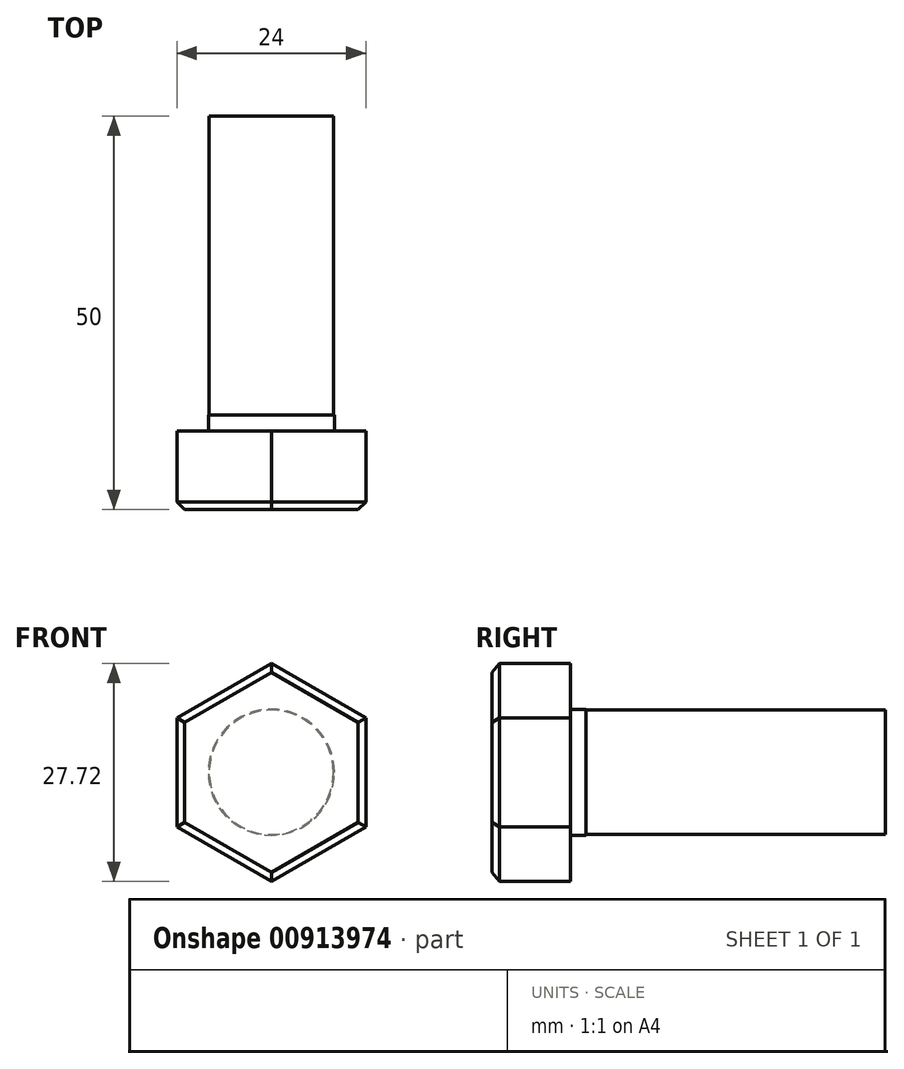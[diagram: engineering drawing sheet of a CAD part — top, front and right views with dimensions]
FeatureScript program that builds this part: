
annotation { "Feature Type Name" : "Feature", "Feature Type Description" : "" }
export const myFeature = defineFeature(function(context is Context, id is Id, definition is map)
    precondition{}
    {
        {
            var Q0;
            Q0=qCreatedBy(makeId("Front.planeOp"),FACE);
            var sketch = newSketch(context, id + "F0", { "sketchPlane" : qUnion([Q0])});
            skLineSegment(sketch, "E0", {"start": v(0, 45.9) * mm, "end": v(0, -43.11) * mm, "construction": true});
            skLineSegment(sketch, "E1", {"start": v(-56.15, 0) * mm, "end": v(55.88, 0) * mm, "construction": true});
            skCircle(sketch, "E2.cCircle", {"center": v(0, 0) * mm, "radius": 12 * mm, "construction": true});
            skLineSegment(sketch, "E2.0", {"start": v(12, -6.93) * mm, "end": v(0, -13.86) * mm});
            skLineSegment(sketch, "E2.1", {"start": v(0, -13.86) * mm, "end": v(-12, -6.93) * mm});
            skLineSegment(sketch, "E2.2", {"start": v(-12, -6.93) * mm, "end": v(-12, 6.93) * mm});
            skLineSegment(sketch, "E2.3", {"start": v(-12, 6.93) * mm, "end": v(0, 13.86) * mm});
            skLineSegment(sketch, "E2.4", {"start": v(0, 13.86) * mm, "end": v(12, 6.93) * mm});
            skLineSegment(sketch, "E2.5", {"start": v(12, 6.93) * mm, "end": v(12, -6.93) * mm});
            skPoint(sketch, "E2.0.midPoint", {"position": v(6, -10.4) * mm});
            skSolve(sketch);
        }
        {
            var Q0;
            Q0=qSketchRegion(id+"F0",true);
            extrude(context, id + "F1", {"entities" : qUnion([Q0]), "depth" : 10 * mm, "offsetDistance" : 25 * mm});
        }
        {
            var Q0;
            Q0=makeQuery(id+"F1.opExtrude","CAP_EDGE",EDGE,{"disambiguationData":[OSD([sQuery(id+"F0.wireOp",EDGE,"E2.4")])],"isStart":false});
            var Q1;
            Q1=makeQuery(id+"F1.opExtrude","CAP_EDGE",EDGE,{"disambiguationData":[OSD([sQuery(id+"F0.wireOp",EDGE,"E2.3")])],"isStart":false});
            var Q2;
            Q2=makeQuery(id+"F1.opExtrude","CAP_EDGE",EDGE,{"disambiguationData":[OSD([sQuery(id+"F0.wireOp",EDGE,"E2.5")])],"isStart":false});
            var Q3;
            Q3=makeQuery(id+"F1.opExtrude","CAP_EDGE",EDGE,{"disambiguationData":[OSD([sQuery(id+"F0.wireOp",EDGE,"E2.0")])],"isStart":false});
            var Q4;
            Q4=makeQuery(id+"F1.opExtrude","CAP_EDGE",EDGE,{"disambiguationData":[OSD([sQuery(id+"F0.wireOp",EDGE,"E2.1")])],"isStart":false});
            var Q5;
            Q5=makeQuery(id+"F1.opExtrude","CAP_EDGE",EDGE,{"disambiguationData":[OSD([sQuery(id+"F0.wireOp",EDGE,"E2.2")])],"isStart":false});
            chamfer(context, id + "F2", {"entities" : qUnion([Q0, Q1, Q2, Q3, Q4, Q5]), "chamferType" : ChamferType.OFFSET_ANGLE, "width" : 1 * mm, "oppositeDirection" : false, "angle" : 45 * degree, "tangentPropagation" : true});
        }
        {
            var Q0;
            Q0=makeQuery(id+"F1.opExtrude","CAP_FACE",FACE,{"disambiguationData":[OSD([sQuery(id+"F0.wireOp",EDGE,"E2.0"),sQuery(id+"F0.wireOp",EDGE,"E2.1"),sQuery(id+"F0.wireOp",EDGE,"E2.2"),sQuery(id+"F0.wireOp",EDGE,"E2.3"),sQuery(id+"F0.wireOp",EDGE,"E2.4"),sQuery(id+"F0.wireOp",EDGE,"E2.5")])],"isStart":true});
            var sketch = newSketch(context, id + "F3", { "sketchPlane" : qUnion([Q0])});
            skCircle(sketch, "E3", {"center": v(0, 0) * mm, "radius": 8 * mm});
            skSolve(sketch);
        }
        {
            var Q0;
            Q0=qSketchRegion(id+"F3",true);
            extrude(context, id + "F4", {"entities" : qUnion([Q0]), "operationType" : NewBodyOperationType.ADD, "depth" : 40 * mm, "offsetDistance" : 25 * mm});
        }
        {
            var Q0;
            Q0=makeQuery(id+"F4.opExtrude","CAP_FACE",FACE,{"disambiguationData":[OSD([sQuery(id+"F3.wireOp",EDGE,"E3")])],"isStart":false});
            var sketch = newSketch(context, id + "F5", { "sketchPlane" : qUnion([Q0])});
            skCircle(sketch, "E4.0", {"center": v(0, 0) * mm, "radius": 7.9 * mm});
            skCircle(sketch, "E5.0", {"center": v(0, 0) * mm, "radius": 8 * mm});
            skSolve(sketch);
        }
        {
            var Q0;
            Q0=qSketchRegion(id+"F5",true);
            extrude(context, id + "F6", {"entities" : qUnion([Q0]), "operationType" : NewBodyOperationType.REMOVE, "oppositeDirection" : true, "depth" : 38 * mm, "offsetDistance" : 25 * mm});
        }
    });
